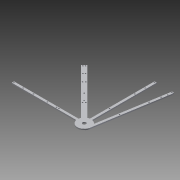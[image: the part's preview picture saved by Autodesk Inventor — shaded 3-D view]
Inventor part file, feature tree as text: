
AUTODESK INVENTOR PART (.ipt)
format: ipt  version: 2013 (Build 170138000, 138)  size: 236,544 bytes
history: native  units: in
note: dims shown in document units (in); Inventor stores cm internally (conversion verified against a paired STEP export)
features: extrude x4, sketch x4, reference x1
ambient origin geometry x8: Origin, YZ Plane, XZ Plane, XY Plane, X Axis, Y Axis, Z Axis, Center Point
feature tree (9):
  extrude  "Extrusion2"  Depth=1.5in
  extrude  "Extrusion8"  Depth=0.25in
  extrude  "Extrusion9"  Depth=2.1762in
  extrude  "Extrusion10"  Depth=0.25in
  sketch  "Sketch1"  dims[d0=0.5in d1=4.0in d2=0.5in d3=0.5in d4=1.5in d5=1.5in d6=1.5in d7=0.25in d8=0.25in d9=0.25in d10=0.5in d11=0.5in d12=3.75in d14=0.266in d15=0.266in d16=0.266in d17=0.25in d18=0.266in d19=0.25in d20=0.25in d21=0.266in d22=0.266in d23=0.266in d24=0.25in d25=0.25in d26=0.266in d28=1.125in d30=0.266in d32=0.266in d33=0.25in d36=1.5in]
  sketch  "Sketch6"  dims[d37=1.0in d38=0.25in]
  sketch  "Sketch8"  dims[d39=5.5in d40=2.1762in]
  sketch  "Sketch9"  dims[d41=5.5in d42=0.25in d43=0.25in d44=0.2874in d45=10.926in d46=10.6389in d47=0.2871in d48=0.2871in d49=15.5in d50=15.5in d51=0.25in d52=0.5in d53=0.266in d54=0.25in d55=0.266in d56=0.266in d57=15.5in d58=0.25in d60=0.266in d61=0.25in d62=0.266in d63=0.266in d64=0.266in d65=0.266in d66=2.0in d67=2.0in d68=2.0in d71=0.297in d72=0.297in d73=0.297in d74=0.297in d75=2.0in d77=0.0in d78=0.25in d79=0.25in d80=0.0in d115=0.266in d117=0.266in d118=9.75in d122=6.0in d123=8.0in d124=0.266in d126=6.0in d127=8.0in d129=0.25in d130=0.25in d131=0.25in d132=0.25in d133=1.0in d134=0.0in d135=0.748in d136=0.25in d137=0.0in d138=1.0in d139=0.0in]
  reference  "Reference1"
